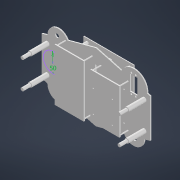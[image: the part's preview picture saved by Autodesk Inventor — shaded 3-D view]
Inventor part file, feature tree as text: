
AUTODESK INVENTOR PART (.ipt)
format: ipt  version: 2021 (Build 250183000, 183)  size: 253,952 bytes
history: native  units: in
note: dims shown in document units (in); Inventor stores cm internally (conversion verified against a paired STEP export)
features: reference x10, sketch x7, other x7, extrude x6
ambient origin geometry x8: Origin, YZ Plane, XZ Plane, XY Plane, X Axis, Y Axis, Z Axis, Center Point
bodies: Solid2 (feature_tree), Solid3 (feature_tree), Solid1 (feature_tree)
feature tree (30):
  extrude  "Extrusion1"  Depth=0.3937in
  extrude  "Extrusion2"  Depth=0.1181in
  extrude  "Extrusion3"  Depth=0.1181in
  extrude  "Extrusion4"  Depth=0.9843in TaperAngle=0.0deg
  extrude  "Extrusion5"  Depth=4.5276in
  extrude  "Extrusion6"  TaperAngle=0.0deg  [1 undecoded]
  sketch  "Sketch7"  dims[d16=0.1181in d17=0.1181in d18=0.1181in d19=0.9843in d20=0.0in d21=3.1496in d22=5.5118in d23=2.9528in d24=5.315in d25=0.1181in d26=0.0in d27=1.9685in]
  sketch  "Sketch1"  dims[d0=0.3937in d1=0.0in d2=2.7559in]
  reference  "Reference1"
  reference  "Reference2"
  reference  "Reference3"
  reference  "Reference4"
  sketch  "Sketch2"  dims[d3=4.3307in d4=0.1181in]
  reference  "Reference5"
  reference  "Reference6"
  sketch  "Sketch3"  dims[d5=0.1181in d6=0.1181in]
  sketch  "Sketch4"  dims[d7=0.1181in d8=0.9843in d9=0.0in]
  reference  "Reference7"
  reference  "Reference8"
  reference  "Reference9"
  reference  "Reference10"
  sketch  "Sketch5"  dims[d10=2.9528in d11=4.5276in]
  sketch  "Sketch6"  dims[d12=0.1181in d13=0.0in d14=0.0in d15=0.0in]
  other  "Solid1:1"
  other  "<path> Marking Bot\Design\iLMbot V3 75%.iam"
  other  "iLMbot V3 75%.iam"
  other  "Arduino Mega ATmega 2560:1"
  other  "Arduino Mega PCB_1"
  other  "RaspberryPi:1"
  other  "Mainboard2_1"
note: 1 required parameter value undecoded (feature->parameter linkage not recoverable at this tier; creation-order binding heuristic only, values carry confidence <= 0.55)
note: 1 file-system path scrubbed to <path> (originals preserved in map.json)
